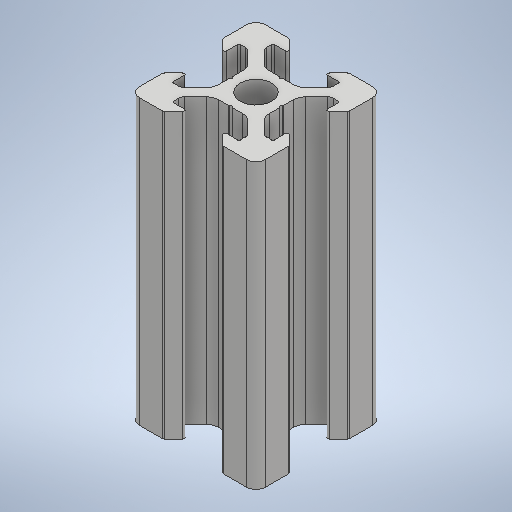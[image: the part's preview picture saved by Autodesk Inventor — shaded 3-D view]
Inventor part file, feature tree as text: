
AUTODESK INVENTOR PART (.ipt)
format: ipt  version: 2025.2 (Build 292293000, 293)  size: 381,952 bytes
history: native  units: mm
features: other x1, extrude x1, sketch x1
ambient origin geometry x8: Origin, YZ Plane, XZ Plane, XY Plane, X Axis, Y Axis, Z Axis, Center Point
bodies: Body1 (feature_tree)
feature tree (3):
  other  "Твердое тело1"
  extrude  "Выдавливание1"  Depth=0.25mm
  sketch  "Эскиз1"
